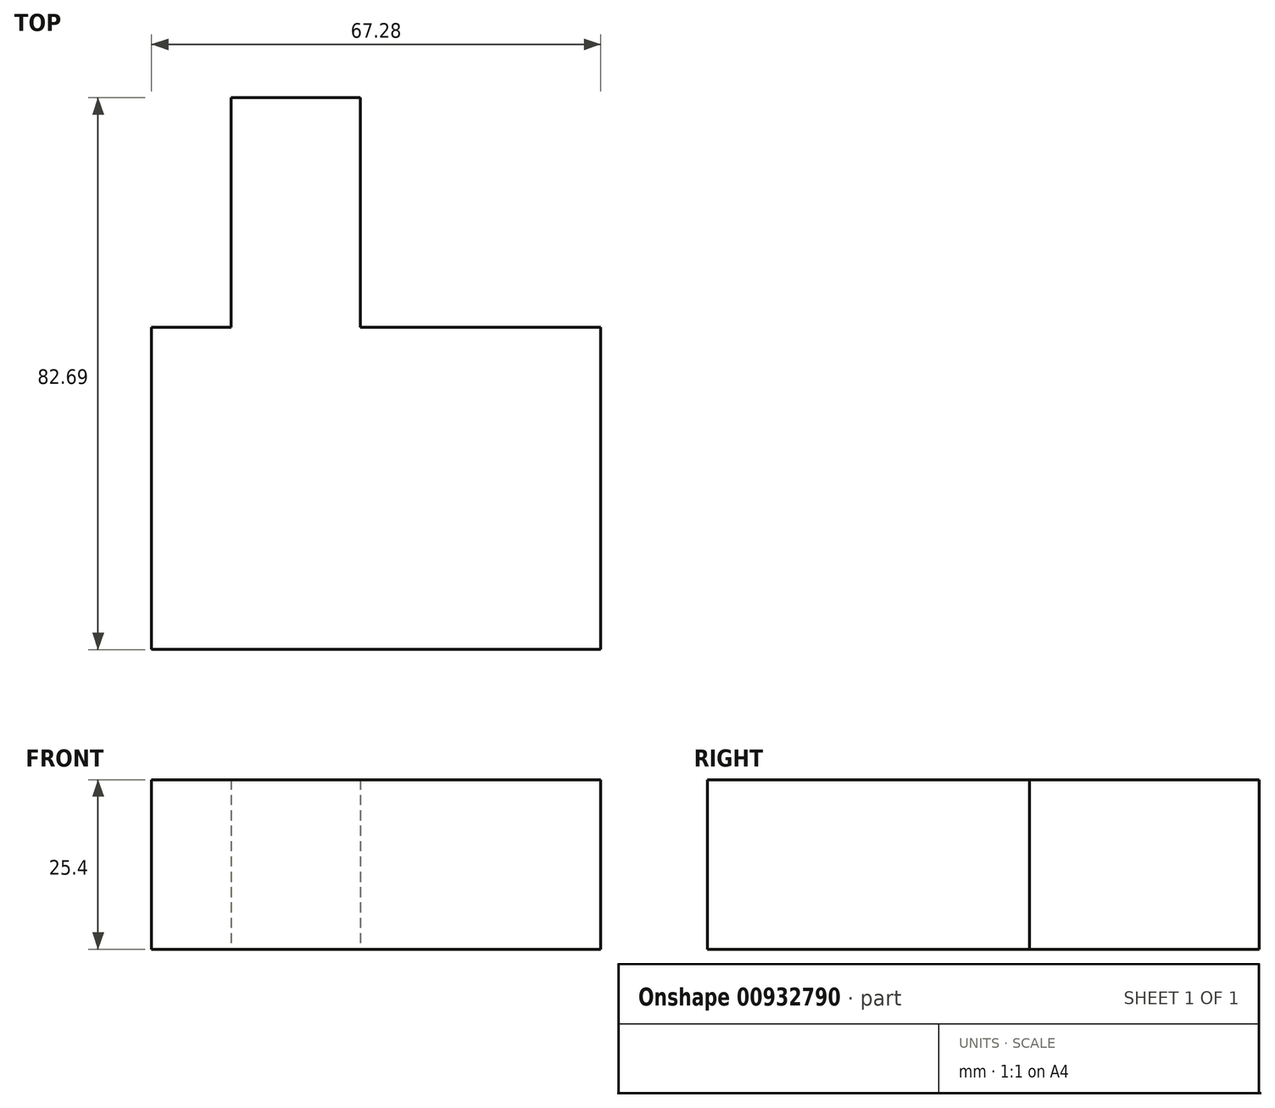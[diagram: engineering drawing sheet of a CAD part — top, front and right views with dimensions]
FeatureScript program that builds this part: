
annotation { "Feature Type Name" : "Feature", "Feature Type Description" : "" }
export const myFeature = defineFeature(function(context is Context, id is Id, definition is map)
    precondition{}
    {
        {
            var Q0;
            Q0=qCreatedBy(makeId("Top.planeOp"),FACE);
            var sketch = newSketch(context, id + "F0", { "sketchPlane" : qUnion([Q0])});
            skLineSegment(sketch, "E0.bottom", {"start": v(-31.29, 0) * mm, "end": v(35.99, 0) * mm});
            skLineSegment(sketch, "E0.top", {"start": v(-31.29, -48.28) * mm, "end": v(35.99, -48.28) * mm});
            skLineSegment(sketch, "E0.left", {"start": v(-31.29, 0) * mm, "end": v(-31.29, -48.28) * mm});
            skLineSegment(sketch, "E0.right", {"start": v(35.99, 0) * mm, "end": v(35.99, -48.28) * mm});
            skLineSegment(sketch, "E1.bottom", {"start": v(0, 0) * mm, "end": v(-19.35, 0) * mm});
            skLineSegment(sketch, "E1.top", {"start": v(0, 34.4) * mm, "end": v(-19.35, 34.4) * mm});
            skLineSegment(sketch, "E1.left", {"start": v(0, 0) * mm, "end": v(0, 34.4) * mm});
            skLineSegment(sketch, "E1.right", {"start": v(-19.35, 0) * mm, "end": v(-19.35, 34.4) * mm});
            skSolve(sketch);
        }
        {
            var Q0;
            Q0 = qSketchRegion(id + "F0", true);
            extrude(context, id + "F1", {"entities" : qUnion([Q0]), "depth" : 25.4 * mm, "offsetDistance" : 25.4 * mm});
        }
    });
